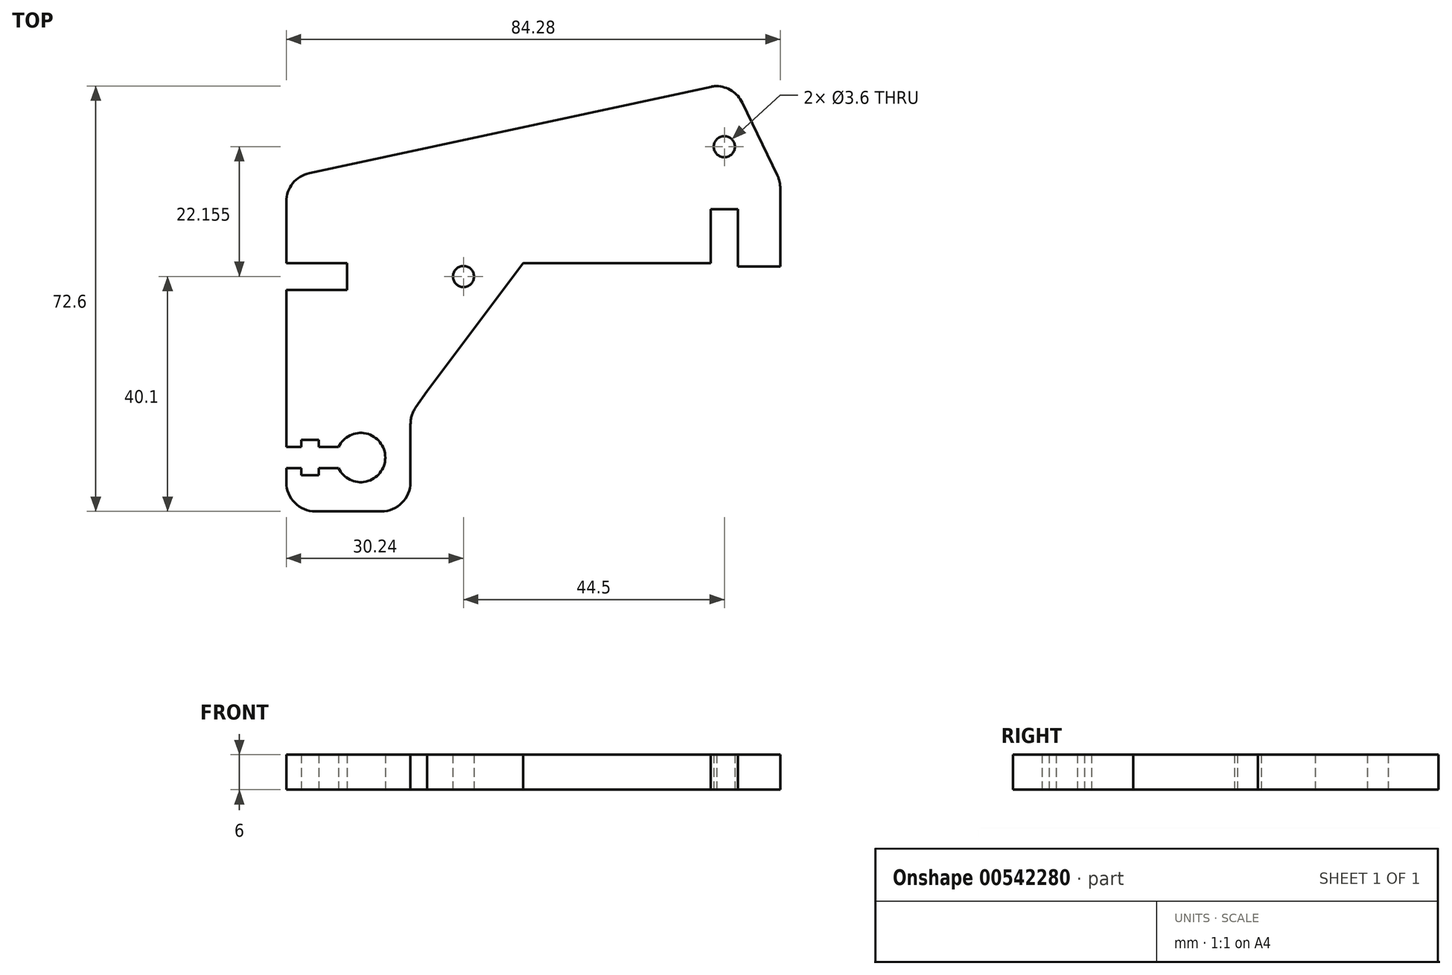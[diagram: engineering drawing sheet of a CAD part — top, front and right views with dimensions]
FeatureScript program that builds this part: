
annotation { "Feature Type Name" : "Feature", "Feature Type Description" : "" }
export const myFeature = defineFeature(function(context is Context, id is Id, definition is map)
    precondition{}
    {
        {
            var Q0;
            Q0=qCreatedBy(makeId("Top.planeOp"),FACE);
            var sketch = newSketch(context, id + "F0", { "sketchPlane" : qUnion([Q0])});
            skCircle(sketch, "E0", {"center": v(-23.12, -30.8) * mm, "radius": 4.2 * mm});
            skCircle(sketch, "E1", {"center": v(38.9, 22.25) * mm, "radius": 1.8 * mm});
            skLineSegment(sketch, "E2", {"start": v(38.9, 22.25) * mm, "end": v(38.9, 7.79) * mm, "construction": true});
            skLineSegment(sketch, "E3", {"start": v(38.9, 11.6) * mm, "end": v(37.1, 11.6) * mm});
            skLineSegment(sketch, "E4", {"start": v(38.9, 11.6) * mm, "end": v(40.7, 11.6) * mm});
            skLineSegment(sketch, "E5", {"start": v(38.9, 22.25) * mm, "end": v(38.9, 32.6) * mm, "construction": true});
            skLineSegment(sketch, "E6", {"start": v(37.47, 32.6) * mm, "end": v(38.9, 32.6) * mm});
            skLineSegment(sketch, "E7", {"start": v(48.45, 1.81) * mm, "end": v(48.45, 15.17) * mm});
            skLineSegment(sketch, "E8", {"start": v(41.97, 29.77) * mm, "end": v(47.95, 17.34) * mm});
            skLineSegment(sketch, "E9", {"start": v(38.9, 32.6) * mm, "end": v(37.74, 32.6) * mm});
            skLineSegment(sketch, "E10", {"start": v(-14.62, -25.1) * mm, "end": v(-14.62, -35) * mm});
            skLineSegment(sketch, "E11", {"start": v(-19.62, -40) * mm, "end": v(-30.83, -40) * mm});
            skLineSegment(sketch, "E12", {"start": v(-35.83, -35) * mm, "end": v(-35.83, -32.6) * mm});
            skLineSegment(sketch, "E13", {"start": v(-25.43, -1.7) * mm, "end": v(-25.43, 1.9) * mm});
            skLineSegment(sketch, "E14", {"start": v(-35.83, 2.4) * mm, "end": v(-35.83, 12.86) * mm});
            skLineSegment(sketch, "E15", {"start": v(-31.88, 17.75) * mm, "end": v(36.7, 32.5) * mm});
            skPoint(sketch, "E16.visualSharp", {"position": v(-35.83, 16.9) * mm});
            skArc(sketch, "E16.filletArc", {"start": v(-31.88, 17.75) * mm, "mid": v(-34.71, 16) * mm, "end": v(-35.83, 12.86) * mm});
            skPoint(sketch, "E17.visualSharp", {"position": v(-35.83, -40) * mm});
            skArc(sketch, "E17.filletArc", {"start": v(-35.83, -35) * mm, "mid": v(-34.36, -38.54) * mm, "end": v(-30.83, -40) * mm});
            skPoint(sketch, "E18.visualSharp", {"position": v(-14.62, -40) * mm});
            skArc(sketch, "E18.filletArc", {"start": v(-19.62, -40) * mm, "mid": v(-16.09, -38.54) * mm, "end": v(-14.63, -35) * mm});
            skPoint(sketch, "E19.visualSharp", {"position": v(-14.62, -20.8) * mm});
            skArc(sketch, "E19.filletArc", {"start": v(-14.6, -23.52) * mm, "mid": v(-14.62, -23.73) * mm, "end": v(-14.62, -23.94) * mm});
            skPoint(sketch, "E20.visualSharp", {"position": v(48.45, 16.31) * mm});
            skArc(sketch, "E20.filletArc", {"start": v(48.45, 15.17) * mm, "mid": v(48.32, 16.29) * mm, "end": v(47.95, 17.34) * mm});
            skPoint(sketch, "E21.visualSharp", {"position": v(37.2, 32.6) * mm});
            skArc(sketch, "E21.filletArc", {"start": v(37.74, 32.6) * mm, "mid": v(37.21, 32.58) * mm, "end": v(36.7, 32.5) * mm});
            skPoint(sketch, "E22.visualSharp", {"position": v(40.6, 32.6) * mm});
            skArc(sketch, "E22.filletArc", {"start": v(41.97, 29.77) * mm, "mid": v(40.13, 31.84) * mm, "end": v(37.47, 32.6) * mm});
            skLineSegment(sketch, "E23", {"start": v(-23.12, -30.8) * mm, "end": v(-23.12, -29) * mm, "construction": true});
            skLineSegment(sketch, "E24", {"start": v(-26.92, -29) * mm, "end": v(-30.26, -29) * mm});
            skLineSegment(sketch, "E25", {"start": v(-23.12, -30.8) * mm, "end": v(-14.62, -30.8) * mm, "construction": true});
            skLineSegment(sketch, "E26", {"start": v(-23.12, -30.8) * mm, "end": v(-23.12, 0) * mm, "construction": true});
            skLineSegment(sketch, "E27", {"start": v(-35.83, -32.6) * mm, "end": v(-33.26, -32.6) * mm});
            skLineSegment(sketch, "E28.trimOffspring", {"start": v(-35.83, -29) * mm, "end": v(-35.83, -2.2) * mm});
            skLineSegment(sketch, "E29", {"start": v(-33.26, -29) * mm, "end": v(-33.26, -27.8) * mm});
            skLineSegment(sketch, "E30", {"start": v(-33.26, -32.6) * mm, "end": v(-33.26, -33.8) * mm});
            skLineSegment(sketch, "E31", {"start": v(-33.26, -27.8) * mm, "end": v(-30.26, -27.8) * mm});
            skLineSegment(sketch, "E32", {"start": v(-30.26, -27.8) * mm, "end": v(-30.26, -29) * mm});
            skLineSegment(sketch, "E33", {"start": v(-33.26, -33.8) * mm, "end": v(-30.26, -33.8) * mm});
            skPoint(sketch, "E34.orphan", {"position": v(-33.26, -30.8) * mm});
            skLineSegment(sketch, "E35.trimOffspring", {"start": v(-30.26, -32.6) * mm, "end": v(-30.26, -33.8) * mm});
            skLineSegment(sketch, "E36.trimOffspring", {"start": v(-33.26, -29) * mm, "end": v(-35.83, -29) * mm});
            skLineSegment(sketch, "E37.trimOffspring", {"start": v(-30.26, -32.6) * mm, "end": v(-26.92, -32.6) * mm});
            skLineSegment(sketch, "E38", {"start": v(38.9, 22.25) * mm, "end": v(-23.12, -30.8) * mm, "construction": true});
            skLineSegment(sketch, "E39", {"start": v(38.9, 22.25) * mm, "end": v(-5.6, 22.25) * mm, "construction": true});
            skLineSegment(sketch, "E40", {"start": v(-25.43, 0.1) * mm, "end": v(7.8, 0.1) * mm, "construction": true});
            skLineSegment(sketch, "E41", {"start": v(-5.6, 22.25) * mm, "end": v(-5.6, -5.85) * mm, "construction": true});
            skCircle(sketch, "E42", {"center": v(-5.6, 0.1) * mm, "radius": 1.8 * mm});
            skLineSegment(sketch, "E43", {"start": v(-35.83, 2.4) * mm, "end": v(-25.43, 2.4) * mm});
            skLineSegment(sketch, "E44", {"start": v(-25.43, 2.4) * mm, "end": v(-25.43, 1.9) * mm});
            skLineSegment(sketch, "E45", {"start": v(-35.83, -2.2) * mm, "end": v(-25.43, -2.2) * mm});
            skLineSegment(sketch, "E46", {"start": v(-25.43, -2.2) * mm, "end": v(-25.43, -1.7) * mm});
            skPoint(sketch, "E47.orphan", {"position": v(-35.83, 1.9) * mm});
            skPoint(sketch, "E48.orphan", {"position": v(-35.83, -1.7) * mm});
            skPoint(sketch, "E49.orphan", {"position": v(37.1, 1.31) * mm});
            skLineSegment(sketch, "E50", {"start": v(41.2, 1.81) * mm, "end": v(48.45, 1.81) * mm});
            skPoint(sketch, "E51.start.orphan", {"position": v(40.7, 1.31) * mm});
            skPoint(sketch, "E52.orphan", {"position": v(48.45, 1.31) * mm});
            skLineSegment(sketch, "E53", {"start": v(36.6, 2.4) * mm, "end": v(36.6, 11.6) * mm});
            skLineSegment(sketch, "E54", {"start": v(36.6, 11.6) * mm, "end": v(37.1, 11.6) * mm});
            skLineSegment(sketch, "E55", {"start": v(41.2, 1.81) * mm, "end": v(41.2, 11.6) * mm});
            skLineSegment(sketch, "E56", {"start": v(41.2, 11.6) * mm, "end": v(40.7, 11.6) * mm});
            skPoint(sketch, "E57.orphan", {"position": v(37.1, 1.81) * mm});
            skPoint(sketch, "E58.orphan", {"position": v(40.7, 1.81) * mm});
            skLineSegment(sketch, "E59", {"start": v(-25.43, 2.4) * mm, "end": v(4.57, 2.4) * mm, "construction": true});
            skLineSegment(sketch, "E60", {"start": v(-11.8, -19.44) * mm, "end": v(4.57, 2.4) * mm});
            skLineSegment(sketch, "E61", {"start": v(4.57, 2.4) * mm, "end": v(36.6, 2.4) * mm});
            skLineSegment(sketch, "E62", {"start": v(-13.75, -22.27) * mm, "end": v(-11.8, -19.44) * mm});
            skArc(sketch, "E63.filletArc", {"start": v(-13.75, -22.27) * mm, "mid": v(-14.4, -23.61) * mm, "end": v(-14.62, -25.1) * mm});
            skSolve(sketch);
        }
        {
            var Q0;
            Q0=makeQuery(id+"F0.imprint","IMPRINT",FACE,{"disambiguationData":[TD([[makeQuery(id+"F0.imprint","IMPRINT",EDGE,{"derivedFrom":sQuery(id+"F0.wireOp",EDGE,"e43Zvh9S-VOie-aNFe-nqfu-2U7vT6FsctXA")}),-1.0]])]});
            var Q1;
            Q1=makeQuery(id+"F0.imprint","IMPRINT",FACE,{"disambiguationData":[TD([[makeQuery(id+"F0.imprint","IMPRINT",EDGE,{"derivedFrom":sQuery(id+"F0.wireOp",EDGE,"E1")}),-1.0]])]});
            extrude(context, id + "F1", {"entities" : qUnion([Q0, Q1]), "depth" : 6 * mm, "offsetDistance" : 25 * mm});
        }
    });
